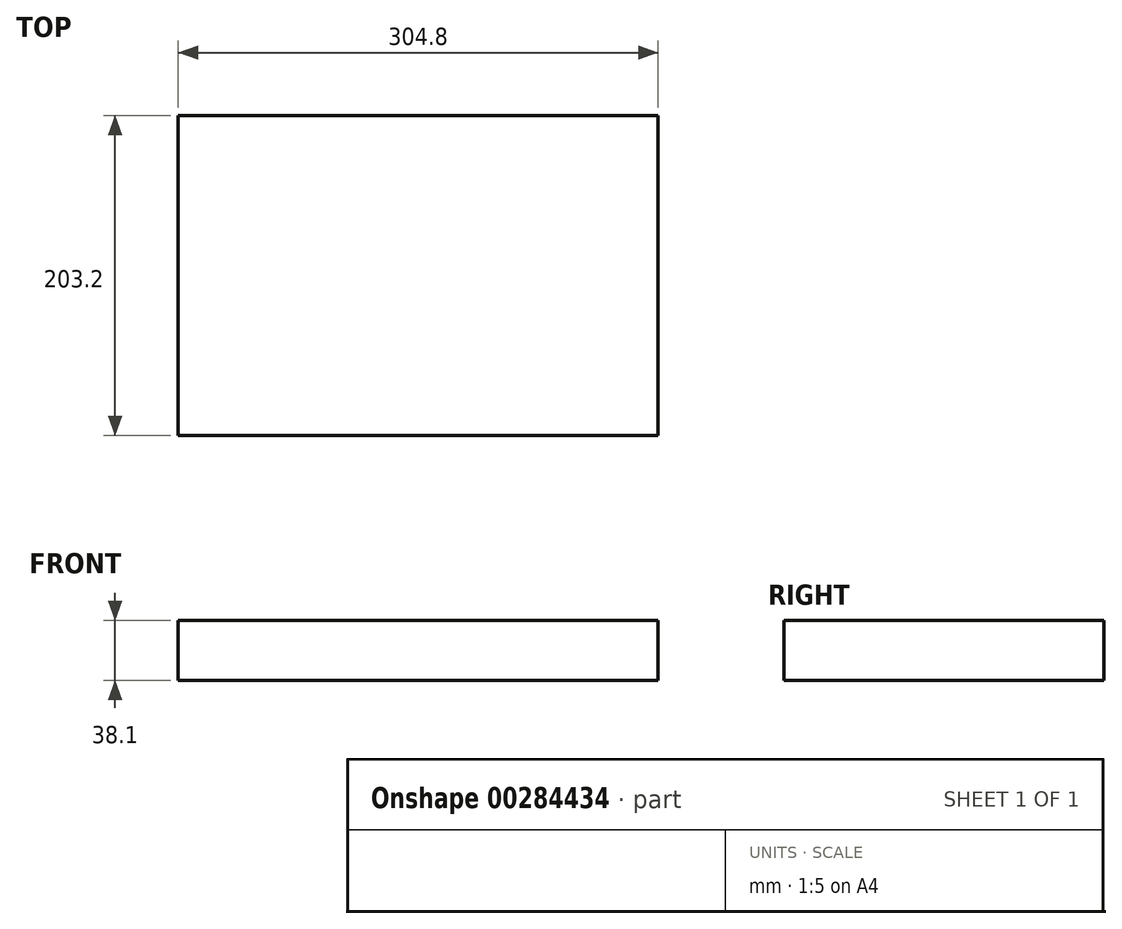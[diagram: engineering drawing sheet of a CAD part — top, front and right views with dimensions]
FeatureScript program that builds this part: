
annotation { "Feature Type Name" : "Feature", "Feature Type Description" : "" }
export const myFeature = defineFeature(function(context is Context, id is Id, definition is map)
    precondition{}
    {
        {
            var Q0;
            Q0=qCreatedBy(makeId("Top.planeOp"),FACE);
            var sketch = newSketch(context, id + "F0", { "sketchPlane" : qUnion([Q0])});
            skLineSegment(sketch, "E0.bottom", {"start": v(-152.4, 101.6) * mm, "end": v(152.4, 101.6) * mm});
            skLineSegment(sketch, "E0.top", {"start": v(-152.4, -101.6) * mm, "end": v(152.4, -101.6) * mm});
            skLineSegment(sketch, "E0.left", {"start": v(-152.4, 101.6) * mm, "end": v(-152.4, -101.6) * mm});
            skLineSegment(sketch, "E0.right", {"start": v(152.4, 101.6) * mm, "end": v(152.4, -101.6) * mm});
            skPoint(sketch, "E0.middle", {"position": v(0, 0) * mm});
            skSolve(sketch);
        }
        {
            var Q0;
            Q0=makeQuery(id+"F0.imprint","IMPRINT",FACE,{"disambiguationData":[TD([[makeQuery(id+"F0.imprint","IMPRINT",EDGE,{"derivedFrom":sQuery(id+"F0.wireOp",EDGE,"E0.bottom")}),-1.0]])]});
            extrude(context, id + "F1", {"entities" : qUnion([Q0]), "depth" : 38.1 * mm});
        }
    });
